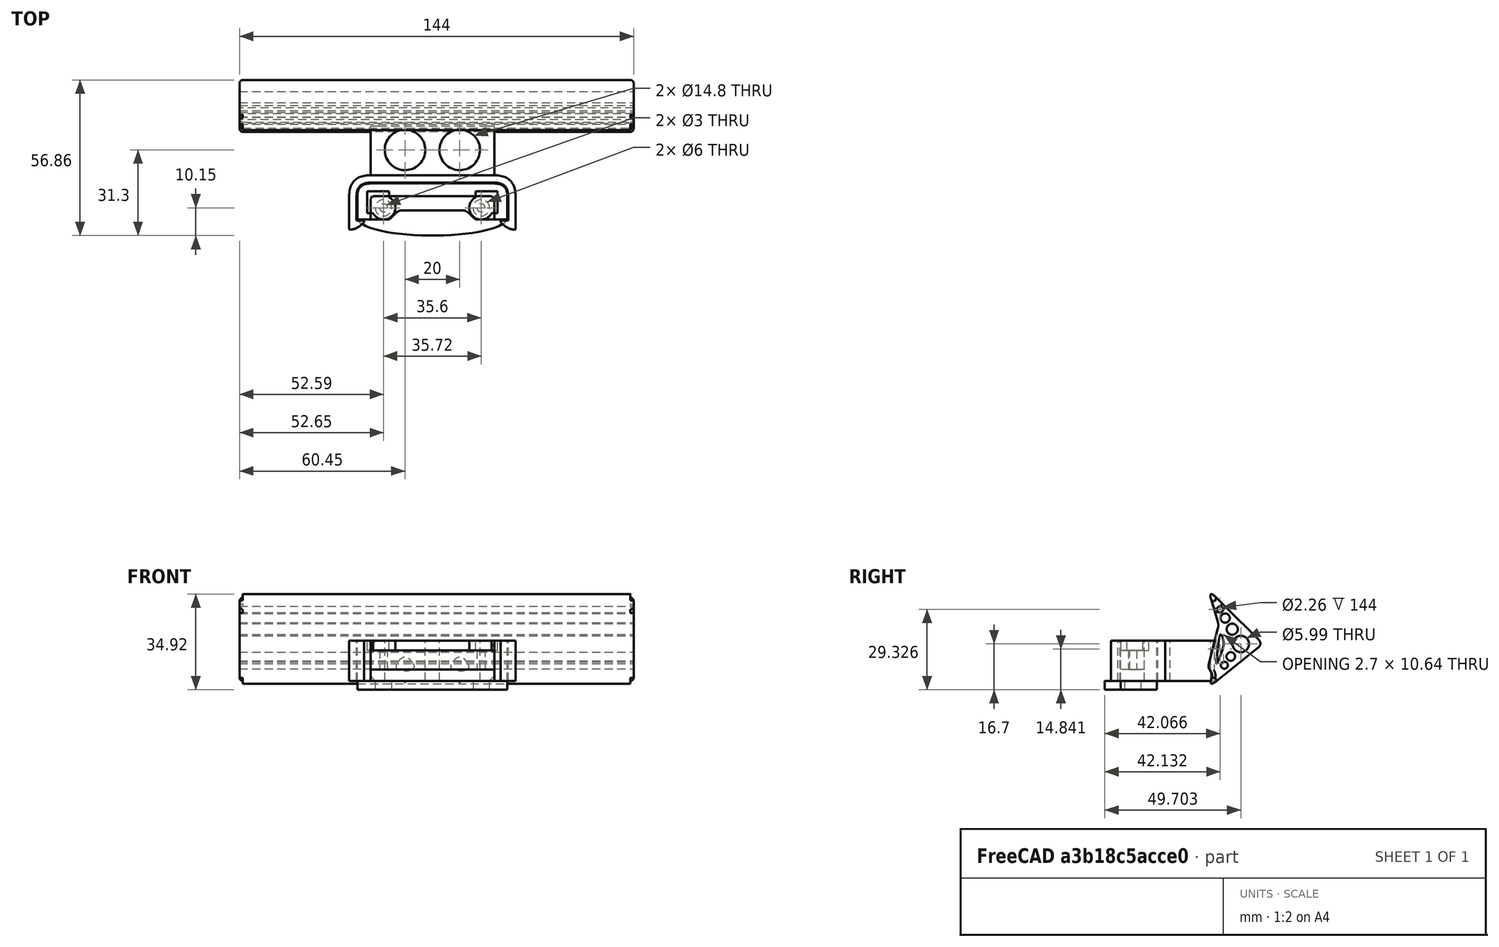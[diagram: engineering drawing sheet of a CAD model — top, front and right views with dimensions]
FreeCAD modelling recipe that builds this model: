
FCSTD DOCUMENT  (FreeCAD 0.19R0.19.2)
Label: 036
License: All rights reserved
LicenseURL: http://en.wikipedia.org/wiki/All_rights_reserved
objects: Sketcher::SketchObject×6, Part::Extrusion×6, Part::Cylinder×4, Part::Fillet×3, Part::MultiFuse×2, Part::Cut×2, Part::Box×1
note: 24 computed .brp shape members not serialized (recipe doc carries the construction recipe); baked Part::Feature solids carry a one-line shape summary decoded from their .brp

FEATURE [Sketcher::SketchObject] Sketch  label="attatchmentPiece"
  FullyConstrained = true
  sketch-geometry (20):
    g0: Circle CenterX=16.25 CenterY=0 CenterZ=0 NormalX=0 NormalY=0 NormalZ=1 AngleXU=0 Radius=1.5
    g1: LineSegment StartX=21.05 StartY=0 StartZ=0 EndX=21.05 EndY=-1 EndZ=0
    g2: LineSegment StartX=21.05 StartY=-1 StartZ=0 EndX=21.05 EndY=-4.3 EndZ=0
    g3: LineSegment StartX=-24.15 StartY=4.3 StartZ=0 EndX=21.05 EndY=4.3 EndZ=0
    g4: LineSegment StartX=21.05 StartY=0 StartZ=0 EndX=21.05 EndY=4.3 EndZ=0
    g5-g8: Circle x4 (B-spline internal-alignment scaffolding for g9; pole/knot coordinates omitted)
    g9: BSplineCurve PolesCount=4 KnotsCount=2 Degree=3 IsPeriodic=0
    g10: GeomPoint X=10.05 Y=-1 Z=0
    g11: GeomPoint X=14.55 Y=-4.3 Z=0
    g12: LineSegment StartX=10.05 StartY=-1 StartZ=0 EndX=-10.05 EndY=-1 EndZ=0
    g13: LineSegment StartX=14.55 StartY=-4.3 StartZ=0 EndX=21.05 EndY=-4.3 EndZ=0
    g14: LineSegment StartX=-24.15 StartY=4.3 StartZ=0 EndX=-24.15 EndY=-4.3 EndZ=0
    g15: LineSegment StartX=-13.15 StartY=-1 StartZ=0 EndX=-10.05 EndY=-1 EndZ=0
    g16: LineSegment StartX=-24.15 StartY=-4.3 StartZ=0 EndX=-19.35 EndY=-4.3 EndZ=0
    g17: Circle CenterX=-19.35 CenterY=0 CenterZ=0 NormalX=0 NormalY=0 NormalZ=1 AngleXU=0 Radius=1.5
    g18: LineSegment StartX=-19.35 StartY=-4.3 StartZ=0 EndX=-17.65 EndY=-4.3 EndZ=0
    g19: BSplineCurve PolesCount=4 KnotsCount=2 Degree=3 IsPeriodic=0
  constraints (41):
    c: Block(g0)
    c: Vertical(g1)
    c: Coincident(g2,g1)
    c: Vertical(g2)
    c: Block(g1)
    c: Horizontal(g3)
    c: Vertical(g4)
    c: Coincident(g4,g3)
    c: Block(g3)
    c: Block(g4)
    c: Weight(g5) = 1
    c: Equal(g5,g6)
    c: Equal(g5,g7)
    c: Equal(g5,g8)
    c: InternalAlignment(g5-g8 -> g9) x4
    c: InternalAlignment(g10,g9)
    c: InternalAlignment(g11,g9)
    c: Block(g9)
    c: Coincident(g12,g9)
    c: Horizontal(g12)
    c: Coincident(g13,g9)
    c: Coincident(g13,g2)
    c: Horizontal(g13)
    c: Distance(g3) = 45.2
    c: Coincident(g14,g3)
    c: Vertical(g14)
    c: Horizontal(g15)
    c: Distance(g15) = 3.1
    c: Block(g17)
    c: Horizontal(g16)
    c: Block(g19)
    c: Coincident(g18,g16)
    c: Coincident(g18,g19)
    c: Horizontal(g18)
    c: Block(g18)
    c: Coincident(g19,g15)
    c: Block(g16)
    c: Block(g12)
    c: Block(g14)
    c: Distance(g16) = 4.8
    c: Distance(g18) = 1.7
FEATURE [Part::Extrusion] Extrude  label="attatchmentPiece001"
  Base = -> Sketch
  Dir = (0,0,1)
  DirMode = 2
  FaceMakerClass = Part::FaceMakerBullseye
  LengthFwd = 7
  LengthRev = 0
  Solid = true
  Symmetric = false
FEATURE [Sketcher::SketchObject] Sketch001  label="attatchmentPieceSurround"
  FullyConstrained = true
  sketch-geometry (18):
    g0: LineSegment StartX=25.85 StartY=-4.3 StartZ=0 EndX=21.05 EndY=-4.3 EndZ=0
    g1: LineSegment StartX=25.85 StartY=-4.3 StartZ=0 EndX=25.85 EndY=4.3 EndZ=0
    g2: LineSegment StartX=-21.05 StartY=8.9 StartZ=0 EndX=21.05 EndY=8.9 EndZ=0
    g3: Circle CenterX=21.05 CenterY=8.9 CenterZ=0 NormalX=0 NormalY=0 NormalZ=1 AngleXU=0 Radius=1
    g4: Circle CenterX=25.85 CenterY=8.9 CenterZ=0 NormalX=0 NormalY=0 NormalZ=1 AngleXU=0 Radius=1
    g5: Circle CenterX=25.85 CenterY=4.3 CenterZ=0 NormalX=0 NormalY=0 NormalZ=1 AngleXU=0 Radius=1
    g6: BSplineCurve PolesCount=3 KnotsCount=2 Degree=2 IsPeriodic=0
    g7: GeomPoint X=21.05 Y=8.9 Z=0
    g8: GeomPoint X=25.85 Y=4.3 Z=0
    g9: ArcOfCircle CenterX=19.45 CenterY=2.7 CenterZ=0 NormalX=0 NormalY=0 NormalZ=1 AngleXU=0 Radius=1.6 StartAngle=0 EndAngle=1.5708
    g10: LineSegment StartX=21.05 StartY=2.7 StartZ=0 EndX=21.05 EndY=-4.3 EndZ=0
    g11: BSplineCurve PolesCount=3 KnotsCount=2 Degree=2 IsPeriodic=0
    g12: LineSegment StartX=-28.95 StartY=-4.3 StartZ=0 EndX=-28.95 EndY=4.3 EndZ=0
    g13: LineSegment StartX=-24.15 StartY=-4.3 StartZ=0 EndX=-28.95 EndY=-4.3 EndZ=0
    g14: LineSegment StartX=-24.15 StartY=2.7 StartZ=0 EndX=-24.15 EndY=-4.3 EndZ=0
    g15: ArcOfCircle CenterX=-22.55 CenterY=2.7 CenterZ=0 NormalX=0 NormalY=0 NormalZ=1 AngleXU=0 Radius=1.6 StartAngle=1.5708 EndAngle=3.14159
    g16: LineSegment StartX=-24.15 StartY=8.9 StartZ=0 EndX=-21.05 EndY=8.9 EndZ=0
    g17: LineSegment StartX=-22.55 StartY=4.3 StartZ=0 EndX=19.45 EndY=4.3 EndZ=0
  constraints (38):
    c: Horizontal(g0)
    c: Vertical(g1)
    c: Coincident(g1,g0)
    c: Horizontal(g2)
    c: Distance(g2) = 42.1
    c: Block(g2)
    c: Coincident(g6,g2)
    c: Weight(g3) = 1
    c: Equal(g3,g4)
    c: Equal(g3,g5)
    c: Coincident(g6,g1)
    c: InternalAlignment(g3,g6)
    c: InternalAlignment(g4,g6)
    c: InternalAlignment(g5,g6)
    c: InternalAlignment(g7,g6)
    c: InternalAlignment(g8,g6)
    c: Block(g0)
    c: Block(g6)
    c: Block(g9)
    c: Coincident(g10,g9)
    c: Coincident(g10,g0)
    c: Vertical(g10)
    c: Horizontal(g13)
    c: Coincident(g12,g13)
    c: Vertical(g12)
    c: Coincident(g11,g12)
    c: Block(g12)
    c: Block(g11)
    c: Block(g15)
    c: Coincident(g14,g15)
    c: Coincident(g14,g13)
    c: Vertical(g14)
    c: Coincident(g16,g11)
    c: Coincident(g16,g2)
    c: Horizontal(g16)
    c: Coincident(g17,g15)
    c: Coincident(g17,g9)
    c: Horizontal(g17)
FEATURE [Part::Extrusion] Extrude001  label="attatchmentPieceSurround001"
  Base = -> Sketch001
  Dir = (0,0,1)
  DirMode = 2
  FaceMakerClass = Part::FaceMakerBullseye
  LengthFwd = 14.7
  LengthRev = 0
  Placement = pos=(0,0,-4.1) rot=(0,0,1;0rad)
  Solid = true
  Symmetric = false
FEATURE [Sketcher::SketchObject] Sketch002  label="attatchmentPieceEndScrewHoleCaps"
  FullyConstrained = true
  sketch-geometry (10):
    g0: ArcOfCircle CenterX=16.25 CenterY=0 CenterZ=0 NormalX=0 NormalY=0 NormalZ=1 AngleXU=0 Radius=4.3 StartAngle=2.05456 EndAngle=5.79942
    g1: LineSegment StartX=14.25 StartY=3.80657 StartZ=0 EndX=14.25 EndY=6 EndZ=0
    g2: LineSegment StartX=20.0566 StartY=-2 StartZ=0 EndX=22.25 EndY=-2 EndZ=0
    g3: LineSegment StartX=22.25 StartY=-2 StartZ=0 EndX=22.25 EndY=6 EndZ=0
    g4: LineSegment StartX=14.25 StartY=6 StartZ=0 EndX=22.25 EndY=6 EndZ=0
    g5: LineSegment StartX=-25.35 StartY=-2 StartZ=0 EndX=-25.35 EndY=6 EndZ=0
    g6: LineSegment StartX=-25.35 StartY=-2 StartZ=0 EndX=-23.1566 EndY=-2 EndZ=0
    g7: LineSegment StartX=-17.35 StartY=6 StartZ=0 EndX=-25.35 EndY=6 EndZ=0
    g8: LineSegment StartX=-17.35 StartY=3.80657 StartZ=0 EndX=-17.35 EndY=6 EndZ=0
    g9: ArcOfCircle CenterX=-19.35 CenterY=0 CenterZ=0 NormalX=0 NormalY=0 NormalZ=1 AngleXU=0 Radius=4.3 StartAngle=3.62536 EndAngle=7.37022
  constraints (25):
    c: Block(g0)
    c: Vertical(g1)
    c: Horizontal(g2)
    c: Coincident(g3,g2)
    c: Vertical(g3)
    c: Coincident(g4,g1)
    c: Horizontal(g4)
    c: Coincident(g3,g4)
    c: Block(g4)
    c: Block(g3)
    c: Coincident(g0,g1)
    c: Coincident(g0,g2)
    c: Block(g1)
    c: Block(g9)
    c: Horizontal(g6)
    c: Vertical(g8)
    c: Coincident(g7,g8)
    c: Horizontal(g7)
    c: Coincident(g5,g6)
    c: Vertical(g5)
    c: Coincident(g5,g7)
    c: Block(g7)
    c: Block(g5)
    c: Coincident(g9,g6)
    c: Coincident(g9,g8)
FEATURE [Part::Extrusion] Extrude002  label="attatchmentPieceEndScrewHoleCaps001"
  Base = -> Sketch002
  Dir = (0,0,1)
  DirMode = 2
  FaceMakerClass = Part::FaceMakerBullseye
  LengthFwd = 3.6
  LengthRev = 0
  Placement = pos=(0,0,7) rot=(0,0,1;0rad)
  Solid = true
  Symmetric = false
FEATURE [Sketcher::SketchObject] Sketch003  label="mainBumpperPieceAttatchment"
  FullyConstrained = true
  sketch-geometry (42):
    g0: Circle CenterX=28.85 CenterY=4.3 CenterZ=0 NormalX=0 NormalY=0 NormalZ=1 AngleXU=0 Radius=1
    g1: Circle CenterX=28.85 CenterY=11.9 CenterZ=0 NormalX=0 NormalY=0 NormalZ=1 AngleXU=0 Radius=1
    g2: Circle CenterX=21.05 CenterY=11.9 CenterZ=0 NormalX=0 NormalY=0 NormalZ=1 AngleXU=0 Radius=1
    g3: BSplineCurve PolesCount=3 KnotsCount=2 Degree=2 IsPeriodic=0
    g4: GeomPoint X=28.85 Y=4.3 Z=0
    g5: GeomPoint X=21.05 Y=11.9 Z=0
    g6: LineSegment StartX=-21.05 StartY=11.9 StartZ=0 EndX=21.05 EndY=11.9 EndZ=0
    g7: LineSegment StartX=28.85 StartY=4.3 StartZ=0 EndX=28.85 EndY=-4.3 EndZ=0
    g8: Circle CenterX=21.05 CenterY=9.2 CenterZ=0 NormalX=0 NormalY=0 NormalZ=1 AngleXU=0 Radius=1
    g9: Circle CenterX=26.15 CenterY=9.2 CenterZ=0 NormalX=0 NormalY=0 NormalZ=1 AngleXU=0 Radius=1
    g10: Circle CenterX=26.15 CenterY=4.3 CenterZ=0 NormalX=0 NormalY=0 NormalZ=1 AngleXU=0 Radius=1
    g11: BSplineCurve PolesCount=3 KnotsCount=2 Degree=2 IsPeriodic=0
    g12: GeomPoint X=21.05 Y=9.2 Z=0
    g13: GeomPoint X=26.15 Y=4.3 Z=0
    g14: LineSegment StartX=-21.05 StartY=9.2 StartZ=0 EndX=21.05 EndY=9.2 EndZ=0
    g15: LineSegment StartX=26.15 StartY=-4.3 StartZ=0 EndX=26.15 EndY=4.3 EndZ=0
    g16: LineSegment StartX=26.15 StartY=-4.3 StartZ=0 EndX=26.15 EndY=-4.6 EndZ=0
    g17: LineSegment StartX=23.45 StartY=-4.6 StartZ=0 EndX=26.15 EndY=-4.6 EndZ=0
    g18: LineSegment StartX=28.85 StartY=-4.3 StartZ=0 EndX=28.85 EndY=-7.9 EndZ=0
    g19: LineSegment StartX=23.45 StartY=-4.6 StartZ=0 EndX=23.45 EndY=-5.3 EndZ=0
    g20: Circle CenterX=28.85 CenterY=-7.9 CenterZ=0 NormalX=0 NormalY=0 NormalZ=1 AngleXU=0 Radius=1
    g21: Circle CenterX=26.15 CenterY=-8.2 CenterZ=0 NormalX=0 NormalY=0 NormalZ=1 AngleXU=0 Radius=1
    g22: Circle CenterX=23.45 CenterY=-5.3 CenterZ=0 NormalX=0 NormalY=0 NormalZ=1 AngleXU=0 Radius=1
    g23: BSplineCurve PolesCount=3 KnotsCount=2 Degree=2 IsPeriodic=0
    g24: GeomPoint X=28.85 Y=-7.9 Z=0
    g25: GeomPoint X=23.45 Y=-5.3 Z=0
    g26: LineSegment StartX=-21.05 StartY=9.2 StartZ=0 EndX=-24.15 EndY=9.2 EndZ=0
    g27: BSplineCurve PolesCount=3 KnotsCount=2 Degree=2 IsPeriodic=0
    g28: LineSegment StartX=-29.25 StartY=-4.3 StartZ=0 EndX=-29.25 EndY=-4.6 EndZ=0
    g29: LineSegment StartX=-29.25 StartY=-4.6 StartZ=0 EndX=-26.55 EndY=-4.6 EndZ=0
    g30: LineSegment StartX=-31.95 StartY=-4.3 StartZ=0 EndX=-31.95 EndY=-7.9 EndZ=0
    g31: LineSegment StartX=-26.55 StartY=-4.6 StartZ=0 EndX=-26.55 EndY=-5.3 EndZ=0
    g32: Circle CenterX=-31.95 CenterY=-7.9 CenterZ=0 NormalX=0 NormalY=0 NormalZ=1 AngleXU=0 Radius=1
    g33: Circle CenterX=-29.25 CenterY=-8.2 CenterZ=0 NormalX=0 NormalY=0 NormalZ=1 AngleXU=0 Radius=1
    g34: Circle CenterX=-26.55 CenterY=-5.3 CenterZ=0 NormalX=0 NormalY=0 NormalZ=1 AngleXU=0 Radius=1
    g35: BSplineCurve PolesCount=3 KnotsCount=2 Degree=2 IsPeriodic=0
    g36: GeomPoint X=-31.95 Y=-7.9 Z=0
    g37: GeomPoint X=-26.55 Y=-5.3 Z=0
    g38: LineSegment StartX=-31.95 StartY=4.3 StartZ=0 EndX=-31.95 EndY=-4.3 EndZ=0
    g39: LineSegment StartX=-29.25 StartY=-4.3 StartZ=0 EndX=-29.25 EndY=4.3 EndZ=0
    g40: BSplineCurve PolesCount=3 KnotsCount=2 Degree=2 IsPeriodic=0
    g41: LineSegment StartX=-21.05 StartY=11.9 StartZ=0 EndX=-24.15 EndY=11.9 EndZ=0
  constraints (78):
    c: Weight(g0) = 1
    c: Equal(g0,g1)
    c: Equal(g0,g2)
    c: InternalAlignment(g0,g3)
    c: InternalAlignment(g1,g3)
    c: InternalAlignment(g2,g3)
    c: InternalAlignment(g4,g3)
    c: InternalAlignment(g5,g3)
    c: Block(g3)
    c: Horizontal(g6)
    c: Vertical(g7)
    c: Block(g7)
    c: Block(g6)
    c: Weight(g8) = 1
    c: Equal(g8,g9)
    c: Equal(g8,g10)
    c: InternalAlignment(g8,g11)
    c: InternalAlignment(g9,g11)
    c: InternalAlignment(g10,g11)
    c: InternalAlignment(g12,g11)
    c: InternalAlignment(g13,g11)
    c: Horizontal(g14)
    c: Vertical(g15)
    c: Block(g11)
    c: Block(g15)
    c: Block(g14)
    c: Coincident(g16,g15)
    c: Vertical(g16)
    c: Distance(g16) = 0.3
    c: Horizontal(g17)
    c: Coincident(g17,g16)
    c: Coincident(g18,g7)
    c: Vertical(g18)
    c: Distance(g18) = 3.6
    c: Vertical(g19)
    c: Coincident(g19,g17)
    c: Coincident(g23,g18)
    c: Weight(g20) = 1
    c: Equal(g20,g21)
    c: Equal(g20,g22)
    c: Coincident(g23,g19)
    c: InternalAlignment(g20,g23)
    c: InternalAlignment(g21,g23)
    c: InternalAlignment(g22,g23)
    c: InternalAlignment(g24,g23)
    c: InternalAlignment(g25,g23)
    c: Block(g23)
    c: Horizontal(g26)
    c: Distance(g26) = 3.1
    c: Block(g27)
    c: Vertical(g38)
    c: Block(g38)
    c: Vertical(g39)
    c: Block(g40)
    c: Block(g39)
    c: Vertical(g28)
    c: Coincident(g28,g39)
    c: Coincident(g29,g28)
    c: Horizontal(g29)
    c: Vertical(g30)
    c: Coincident(g30,g38)
    c: Coincident(g31,g29)
    c: Vertical(g31)
    c: Coincident(g35,g30)
    c: Equal(g32,g33)
    c: Equal(g32,g34)
    c: Coincident(g35,g31)
    c: InternalAlignment(g32,g35)
    c: InternalAlignment(g33,g35)
    c: InternalAlignment(g34,g35)
    c: InternalAlignment(g36,g35)
    c: InternalAlignment(g37,g35)
    c: Block(g35)
    c: Coincident(g40,g26)
    c: Block(g29)
    c: Horizontal(g41)
    c: Equal(g26,g41) = 3.1
    c: Coincident(g41,g6)
FEATURE [Part::Box] Box  label="bumpperExtension"
  AttacherType = Attacher::AttachEngine3D
  Height = 14.7
  Length = 45.2
  Placement = pos=(-24.15,11.9,-4.1) rot=(0,0,1;0rad)
  Width = 18
FEATURE [Sketcher::SketchObject] Sketch004  label="bumpperMain"
  FullyConstrained = true
  Placement = pos=(0,0,0) rot=(0.57735,0.57735,0.57735;2.0944rad)
  sketch-geometry (62):
    g0: Circle CenterX=-3.12329 CenterY=2.49901 CenterZ=0 NormalX=0 NormalY=0 NormalZ=1 AngleXU=0 Radius=1
    g1: Circle CenterX=0 CenterY=0 CenterZ=0 NormalX=0 NormalY=0 NormalZ=1 AngleXU=0 Radius=1
    g2: Circle CenterX=-1.35243 CenterY=3.60648 CenterZ=0 NormalX=0 NormalY=0 NormalZ=1 AngleXU=0 Radius=1
    g3: BSplineCurve PolesCount=3 KnotsCount=2 Degree=2 IsPeriodic=0
    g4: GeomPoint X=-3.12329 Y=2.49901 Z=0
    g5: GeomPoint X=-1.35243 Y=3.60648 Z=0
    g6: Circle CenterX=-2.83953 CenterY=33.0261 CenterZ=0 NormalX=0 NormalY=0 NormalZ=1 AngleXU=0 Radius=1
    g7: Circle CenterX=0 CenterY=35.8434 CenterZ=0 NormalX=0 NormalY=0 NormalZ=1 AngleXU=0 Radius=1
    g8: Circle CenterX=-1.15771 CenterY=32.0146 CenterZ=0 NormalX=0 NormalY=0 NormalZ=1 AngleXU=0 Radius=1
    g9: BSplineCurve PolesCount=3 KnotsCount=2 Degree=2 IsPeriodic=0
    g10: GeomPoint X=-2.83953 Y=33.0261 Z=0
    g11: GeomPoint X=-1.15771 Y=32.0146 Z=0
    g12: Circle CenterX=-18.2963 CenterY=17.6904 CenterZ=0 NormalX=0 NormalY=0 NormalZ=1 AngleXU=0 Radius=1
    g13: Circle CenterX=-20 CenterY=16 CenterZ=0 NormalX=0 NormalY=0 NormalZ=1 AngleXU=0 Radius=1
    g14: Circle CenterX=-18.1259 CenterY=14.5008 CenterZ=0 NormalX=0 NormalY=0 NormalZ=1 AngleXU=0 Radius=1
    g15: BSplineCurve PolesCount=3 KnotsCount=2 Degree=2 IsPeriodic=0
    g16: GeomPoint X=-18.2963 Y=17.6904 Z=0
    g17: GeomPoint X=-18.1259 Y=14.5008 Z=0
    g18: LineSegment StartX=-18.2963 StartY=17.6904 StartZ=0 EndX=-2.83953 EndY=33.0261 EndZ=0
    g19: LineSegment StartX=-18.1259 StartY=14.5008 StartZ=0 EndX=-3.12329 EndY=2.49901 EndZ=0
    g20: Circle CenterX=-11.9527 CenterY=16 CenterZ=0 NormalX=0 NormalY=0 NormalZ=1 AngleXU=0 Radius=2.99582
    g21: Circle CenterX=-8.803 CenterY=21.3731 CenterZ=0 NormalX=0 NormalY=0 NormalZ=1 AngleXU=0 Radius=2.03939
    g22: Circle CenterX=-6.23123 CenterY=25.4475 CenterZ=0 NormalX=0 NormalY=0 NormalZ=1 AngleXU=0 Radius=1.69309
    g23: Circle CenterX=-4.38186 CenterY=28.6261 CenterZ=0 NormalX=0 NormalY=0 NormalZ=1 AngleXU=0 Radius=1.13029
    g24: Circle CenterX=-8.28033 CenterY=11.4296 CenterZ=0 NormalX=0 NormalY=0 NormalZ=1 AngleXU=0 Radius=1.57213
    g25: Circle CenterX=-5.93972 CenterY=8.22213 CenterZ=0 NormalX=0 NormalY=0 NormalZ=1 AngleXU=0 Radius=1.28743
    g26: Circle CenterX=-3.47023 CenterY=24.3665 CenterZ=0 NormalX=0 NormalY=0 NormalZ=1 AngleXU=0 Radius=1
    g27: Circle CenterX=-3.90437 CenterY=22.9307 CenterZ=0 NormalX=0 NormalY=0 NormalZ=1 AngleXU=0 Radius=1
    g28: Circle CenterX=-3.53772 CenterY=21.4762 CenterZ=0 NormalX=0 NormalY=0 NormalZ=1 AngleXU=0 Radius=1
    g29: BSplineCurve PolesCount=3 KnotsCount=2 Degree=2 IsPeriodic=0
    g30: GeomPoint X=-3.47023 Y=24.3665 Z=0
    g31: GeomPoint X=-3.53772 Y=21.4762 Z=0
    g32: LineSegment StartX=-1.15771 StartY=32.0146 StartZ=0 EndX=-3.47023 EndY=24.3665 EndZ=0
    g33: Circle CenterX=-5.41867 CenterY=17.9226 CenterZ=0 NormalX=0 NormalY=0 NormalZ=1 AngleXU=0 Radius=1
    g34: Circle CenterX=-6 CenterY=16 CenterZ=0 NormalX=0 NormalY=0 NormalZ=1 AngleXU=0 Radius=1
    g35: Circle CenterX=-5.22753 CenterY=13.9401 CenterZ=0 NormalX=0 NormalY=0 NormalZ=1 AngleXU=0 Radius=1
    g36: BSplineCurve PolesCount=3 KnotsCount=2 Degree=2 IsPeriodic=0
    g37: GeomPoint X=-5.41867 Y=17.9226 Z=0
    g38: GeomPoint X=-5.22753 Y=13.9401 Z=0
    g39: Circle CenterX=-3.98946 CenterY=10.6386 CenterZ=0 NormalX=0 NormalY=0 NormalZ=1 AngleXU=0 Radius=1
    g40: Circle CenterX=-2.58497 CenterY=6.89324 CenterZ=0 NormalX=0 NormalY=0 NormalZ=1 AngleXU=0 Radius=1
    g41: Circle CenterX=-3.11001 CenterY=10.8586 CenterZ=0 NormalX=0 NormalY=0 NormalZ=1 AngleXU=0 Radius=1
    g42: BSplineCurve PolesCount=3 KnotsCount=2 Degree=2 IsPeriodic=0
    g43: GeomPoint X=-3.98946 Y=10.6386 Z=0
    g44: GeomPoint X=-3.11001 Y=10.8586 Z=0
    g45: Circle CenterX=-1.35243 CenterY=3.60648 CenterZ=0 NormalX=0 NormalY=0 NormalZ=1 AngleXU=0 Radius=1
    g46: Circle CenterX=-1.76142 CenterY=4.69712 CenterZ=0 NormalX=0 NormalY=0 NormalZ=1 AngleXU=0 Radius=1
    g47: Circle CenterX=-1.05937 CenterY=5.79125 CenterZ=0 NormalX=0 NormalY=0 NormalZ=1 AngleXU=0 Radius=1
    g48: BSplineCurve PolesCount=3 KnotsCount=2 Degree=2 IsPeriodic=0
    g49: GeomPoint X=-1.35243 Y=3.60648 Z=0
    g50: GeomPoint X=-1.05937 Y=5.79125 Z=0
    g51: Circle CenterX=-0.519336 CenterY=6.6329 CenterZ=0 NormalX=0 NormalY=0 NormalZ=1 AngleXU=0 Radius=1
    g52: Circle CenterX=0 CenterY=7.44228 CenterZ=0 NormalX=0 NormalY=0 NormalZ=1 AngleXU=0 Radius=1
    g53: Circle CenterX=-0.244436 CenterY=8.41194 CenterZ=0 NormalX=0 NormalY=0 NormalZ=1 AngleXU=0 Radius=1
    g54: BSplineCurve PolesCount=3 KnotsCount=2 Degree=2 IsPeriodic=0
    g55: GeomPoint X=-0.519336 Y=6.6329 Z=0
    g56: GeomPoint X=-0.244436 Y=8.41194 Z=0
    g57: LineSegment StartX=-3.53772 StartY=21.4762 StartZ=0 EndX=-0.244436 EndY=8.41194 EndZ=0
    g58: LineSegment StartX=-5.22753 StartY=13.9401 StartZ=0 EndX=-3.98946 EndY=10.6386 EndZ=0
    g59: LineSegment StartX=-1.05937 StartY=5.79125 StartZ=0 EndX=-0.519336 EndY=6.6329 EndZ=0
    g60: BSplineCurve PolesCount=3 KnotsCount=2 Degree=2 IsPeriodic=0
    g61: LineSegment StartX=-4.0304 StartY=17.8099 StartZ=0 EndX=-3.11001 EndY=10.8586 EndZ=0
  constraints (96):
    c: Weight(g0) = 1
    c: Equal(g0,g1)
    c: Equal(g0,g2)
    c: InternalAlignment(g0,g3)
    c: InternalAlignment(g1,g3)
    c: InternalAlignment(g2,g3)
    c: InternalAlignment(g4,g3)
    c: InternalAlignment(g5,g3)
    c: Block(g3)
    c: Weight(g6) = 1
    c: Equal(g6,g7)
    c: Equal(g6,g8)
    c: InternalAlignment(g6,g9)
    c: InternalAlignment(g7,g9)
    c: InternalAlignment(g8,g9)
    c: InternalAlignment(g10,g9)
    c: InternalAlignment(g11,g9)
    c: Block(g9)
    c: Weight(g12) = 1
    c: Equal(g12,g13)
    c: Equal(g12,g14)
    c: InternalAlignment(g12,g15)
    c: InternalAlignment(g13,g15)
    c: InternalAlignment(g14,g15)
    c: InternalAlignment(g16,g15)
    c: InternalAlignment(g17,g15)
    c: Block(g15)
    c: Coincident(g18,g15)
    c: Coincident(g18,g9)
    c: Coincident(g19,g15)
    c: Coincident(g19,g3)
    c: Block(g25)
    c: Block(g24)
    c: Block(g20)
    c: Block(g21)
    c: Block(g22)
    c: Block(g23)
    c: Weight(g26) = 1
    c: Equal(g26,g27)
    c: Equal(g26,g28)
    c: InternalAlignment(g26,g29)
    c: InternalAlignment(g27,g29)
    c: InternalAlignment(g28,g29)
    c: InternalAlignment(g30,g29)
    c: InternalAlignment(g31,g29)
    c: Block(g29)
    c: Coincident(g32,g9)
    c: Coincident(g32,g29)
    c: Weight(g33) = 1
    c: Equal(g33,g34)
    c: Equal(g33,g35)
    c: InternalAlignment(g33,g36)
    c: InternalAlignment(g34,g36)
    c: InternalAlignment(g35,g36)
    c: InternalAlignment(g37,g36)
    c: InternalAlignment(g38,g36)
    c: Block(g36)
    c: Weight(g39) = 1
    c: Equal(g39,g40)
    c: Equal(g39,g41)
    c: InternalAlignment(g39,g42)
    c: InternalAlignment(g40,g42)
    c: InternalAlignment(g41,g42)
    c: InternalAlignment(g43,g42)
    c: InternalAlignment(g44,g42)
    c: Block(g42)
    c: Coincident(g48,g3)
    c: Weight(g45) = 1
    c: Equal(g45,g46)
    c: Equal(g45,g47)
    c: InternalAlignment(g45,g48)
    c: InternalAlignment(g46,g48)
    c: InternalAlignment(g47,g48)
    c: InternalAlignment(g49,g48)
    c: InternalAlignment(g50,g48)
    c: Block(g48)
    c: Weight(g51) = 1
    c: Equal(g51,g52)
    c: Equal(g51,g53)
    c: InternalAlignment(g51,g54)
    c: InternalAlignment(g52,g54)
    c: InternalAlignment(g53,g54)
    c: InternalAlignment(g55,g54)
    c: InternalAlignment(g56,g54)
    c: Block(g54)
    c: Coincident(g57,g29)
    c: Coincident(g57,g54)
    c: Block(g57)
    c: Coincident(g58,g36)
    c: Coincident(g58,g42)
    c: Coincident(g59,g48)
    c: Coincident(g59,g54)
    c: Block(g60)
    c: Coincident(g60,g36)
    c: Coincident(g61,g60)
    c: Coincident(g61,g42)
FEATURE [Part::Extrusion] Extrude004  label="bumpperMain001"
  Base = -> Sketch004
  Dir = (1,0,0)
  DirMode = 2
  FaceMakerClass = Part::FaceMakerBullseye
  LengthFwd = 144
  LengthRev = 0
  Placement = pos=(72,27.6,-6.6) rot=(0,0,1;3.14159rad)
  Solid = true
  Symmetric = false
FEATURE [Sketcher::SketchObject] Sketch005  label="attatchmentPieceBottom"
  FullyConstrained = true
  sketch-geometry (20):
    g0: LineSegment StartX=25.85 StartY=-4.3 StartZ=0 EndX=25.85 EndY=4.3 EndZ=0
    g1: LineSegment StartX=-21.05 StartY=8.9 StartZ=0 EndX=21.05 EndY=8.9 EndZ=0
    g2: Circle CenterX=21.05 CenterY=8.9 CenterZ=0 NormalX=0 NormalY=0 NormalZ=1 AngleXU=0 Radius=1
    g3: Circle CenterX=25.85 CenterY=8.9 CenterZ=0 NormalX=0 NormalY=0 NormalZ=1 AngleXU=0 Radius=1
    g4: Circle CenterX=25.85 CenterY=4.3 CenterZ=0 NormalX=0 NormalY=0 NormalZ=1 AngleXU=0 Radius=1
    g5: BSplineCurve PolesCount=3 KnotsCount=2 Degree=2 IsPeriodic=0
    g6: GeomPoint X=21.05 Y=8.9 Z=0
    g7: GeomPoint X=25.85 Y=4.3 Z=0
    g8: BSplineCurve PolesCount=3 KnotsCount=2 Degree=2 IsPeriodic=0
    g9: LineSegment StartX=-28.95 StartY=-4.3 StartZ=0 EndX=-28.95 EndY=4.3 EndZ=0
    g10: LineSegment StartX=-24.15 StartY=8.9 StartZ=0 EndX=-21.05 EndY=8.9 EndZ=0
    g11: Circle CenterX=-19.41 CenterY=0 CenterZ=0 NormalX=0 NormalY=0 NormalZ=1 AngleXU=0 Radius=3
    g12: Circle CenterX=16.3103 CenterY=0 CenterZ=0 NormalX=0 NormalY=0 NormalZ=1 AngleXU=0 Radius=3
    g13-g16: Circle x4 (B-spline internal-alignment scaffolding for g17; pole/knot coordinates omitted)
    g17: BSplineCurve PolesCount=4 KnotsCount=2 Degree=3 IsPeriodic=0
    g18: GeomPoint X=-28.95 Y=-4.3 Z=0
    g19: GeomPoint X=25.85 Y=-4.3 Z=0
  constraints (36):
    c: Vertical(g0)
    c: Horizontal(g1)
    c: Distance(g1) = 42.1
    c: Block(g1)
    c: Coincident(g5,g1)
    c: Weight(g2) = 1
    c: Equal(g2,g3)
    c: Equal(g2,g4)
    c: Coincident(g5,g0)
    c: InternalAlignment(g2,g5)
    c: InternalAlignment(g3,g5)
    c: InternalAlignment(g4,g5)
    c: InternalAlignment(g6,g5)
    c: InternalAlignment(g7,g5)
    c: Block(g5)
    c: Vertical(g9)
    c: Coincident(g8,g9)
    c: Block(g9)
    c: Block(g8)
    c: Coincident(g10,g8)
    c: Coincident(g10,g1)
    c: Horizontal(g10)
    c: PointOnObject(g12,g-1)
    c: PointOnObject(g11,g-1)
    c: Block(g11)
    c: Block(g12)
    c: Coincident(g17,g9)
    c: Weight(g13) = 1
    c: Equal(g13,g14)
    c: Equal(g13,g15)
    c: Equal(g13,g16)
    c: Coincident(g17,g0)
    c: InternalAlignment(g13-g16 -> g17) x4
    c: InternalAlignment(g18,g17)
    c: InternalAlignment(g19,g17)
    c: Block(g17)
FEATURE [Part::Extrusion] Extrude005  label="attatchmentPieceBottom001"
  Base = -> Sketch005
  Dir = (0,0,1)
  DirMode = 2
  FaceMakerClass = Part::FaceMakerBullseye
  LengthFwd = 3.2
  LengthRev = 0
  Placement = pos=(0,0,-7.3) rot=(0,0,1;0rad)
  Solid = true
  Symmetric = false
FEATURE [Part::Extrusion] Extrude006  label="mainBumpperPieceAttatchment001"
  Base = -> Sketch003
  Dir = (0,0,1)
  DirMode = 2
  FaceMakerClass = Part::FaceMakerBullseye
  LengthFwd = 14.7
  LengthRev = 0
  Placement = pos=(0,0,-4.1) rot=(0,0,1;0rad)
  Solid = true
  Symmetric = false
FEATURE [Part::Cylinder] Cylinder  label="removeFromBumpperExtension"
  Angle = 360
  AttacherType = Attacher::AttachEngine3D
  Height = 20
  Placement = pos=(8.45,21.15,-8) rot=(0,0,1;0rad)
  Radius = 7.4
FEATURE [Part::Cylinder] Cylinder001  label="removeFromBumpperExtension001"
  Angle = 360
  AttacherType = Attacher::AttachEngine3D
  Height = 20
  Placement = pos=(-11.55,21.15,-8) rot=(0,0,1;0rad)
  Radius = 7.4
FEATURE [Part::MultiFuse] Fusion  label="removeFromBumpperExtension002"
  Shapes = -> [Cylinder,Cylinder001]
FEATURE [Part::Cylinder] Cylinder002  label="removeFromBumpperExtension004"
  Angle = 360
  AttacherType = Attacher::AttachEngine3D
  Height = 20
  Placement = pos=(8.45,21.15,-8) rot=(0,0,1;0rad)
  Radius = 7.4
FEATURE [Part::Cylinder] Cylinder003  label="removeFromBumpperExtension005"
  Angle = 360
  AttacherType = Attacher::AttachEngine3D
  Height = 20
  Placement = pos=(-11.55,21.15,-8) rot=(0,0,1;0rad)
  Radius = 7.4
FEATURE [Part::MultiFuse] Fusion001  label="removeFromBumpperMain"
  Shapes = -> [Cylinder002,Cylinder003]
FEATURE [Part::Cut] Cut  label="bumpperExtension001"
  Base = -> Box
  Tool = -> Fusion
FEATURE [Part::Cut] Cut001  label="bumpperMain002"
  Base = -> Extrude004
  Tool = -> Fusion001
FEATURE [Part::Fillet] Fillet  label="bumpperExtension002"
  Base = -> Cut
  Edges = 4 edges r=3: [Edge2,Edge4,Edge9,Edge14]
FEATURE [Part::Fillet] Fillet001
  Base = -> Cut001
  Edges = 11 edges r=1.2: [Edge4,Edge7,Edge10,Edge30,Edge31,Edge32,Edge33,Edge34,Edge35,Edge36,Edge37]
FEATURE [Part::Fillet] Fillet002  label="bumpperMain003"
  Base = -> Fillet001
  Edges = 11 edges r=1.2: [Edge4,Edge9,Edge13,Edge14,Edge15,Edge16,Edge17,Edge18,Edge19,Edge20,Edge21]
